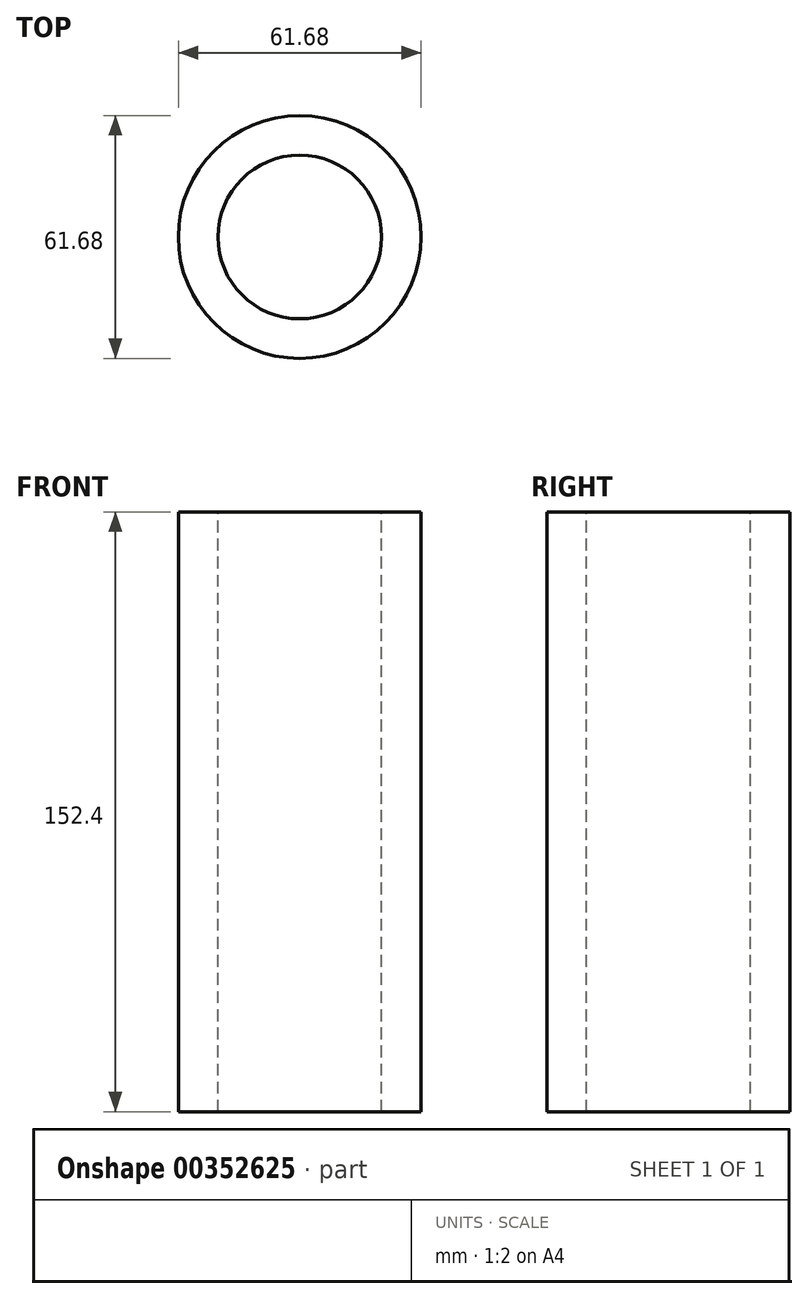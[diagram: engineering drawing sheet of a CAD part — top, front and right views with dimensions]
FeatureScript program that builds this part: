
annotation { "Feature Type Name" : "Feature", "Feature Type Description" : "" }
export const myFeature = defineFeature(function(context is Context, id is Id, definition is map)
    precondition{}
    {
        {
            var Q0;
            Q0=qCreatedBy(makeId("Top.planeOp"),FACE);
            var sketch = newSketch(context, id + "F0", { "sketchPlane" : qUnion([Q0])});
            skCircle(sketch, "E0", {"center": v(0, 0) * mm, "radius": 20.8 * mm});
            skCircle(sketch, "E1", {"center": v(0, 0) * mm, "radius": 30.84 * mm});
            skSolve(sketch);
        }
        {
            var Q0;
            Q0=sQuery(id+"F0.wireOp",EDGE,"E0");
            var Q1;
            Q1=sQuery(id+"F0.wireOp",EDGE,"E1");
            extrude(context, id + "F1", {"bodyType" : ToolBodyType.SURFACE, "surfaceEntities" : qUnion([Q0, Q1]), "depth" : 152.4 * mm});
        }
    });
